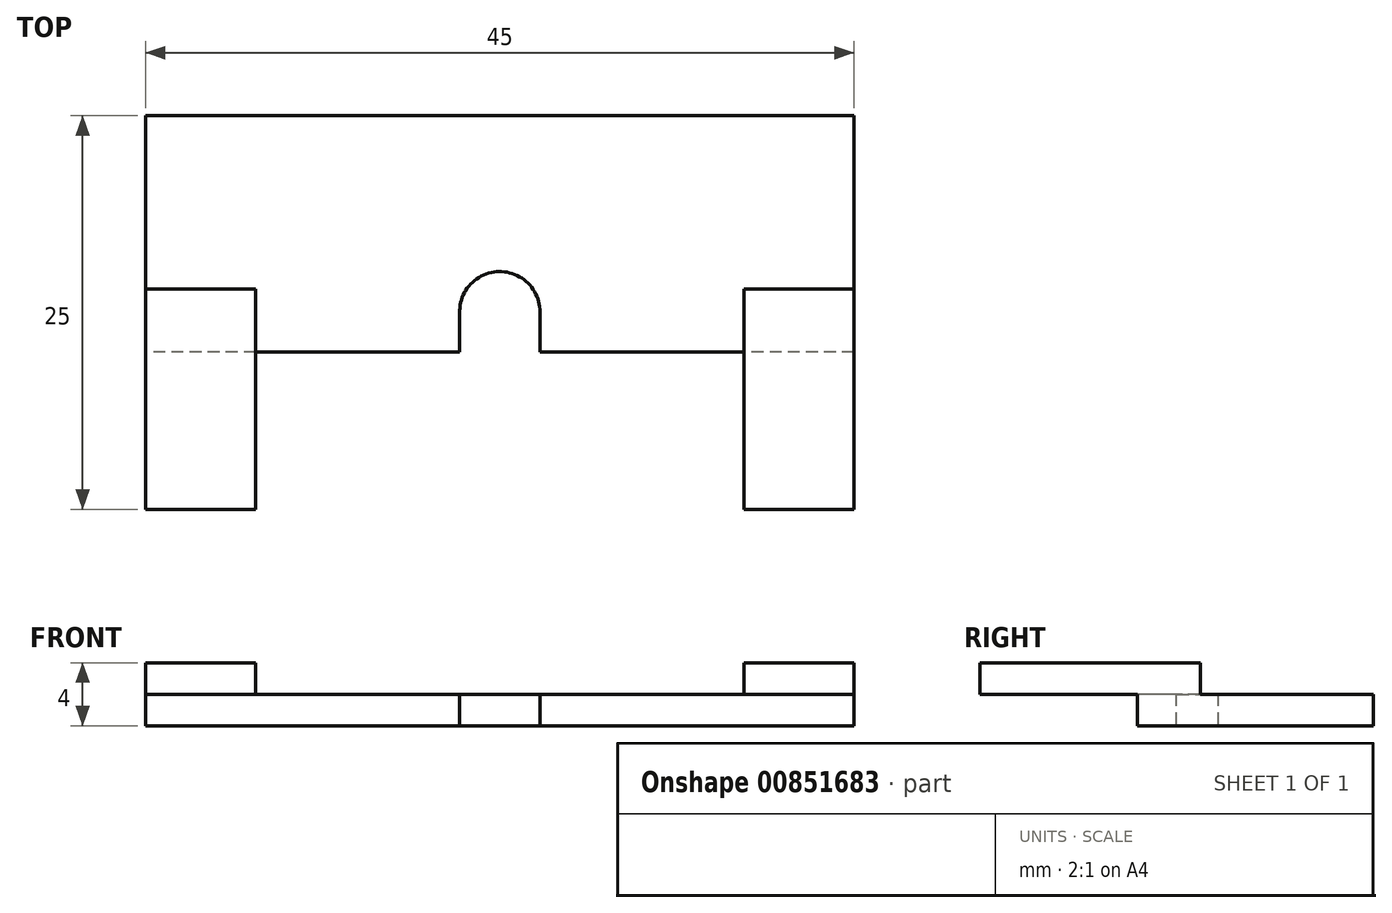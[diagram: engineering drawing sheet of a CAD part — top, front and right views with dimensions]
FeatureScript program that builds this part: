
annotation { "Feature Type Name" : "Feature", "Feature Type Description" : "" }
export const myFeature = defineFeature(function(context is Context, id is Id, definition is map)
    precondition{}
    {
        {
            var Q0;
            Q0=qCreatedBy(makeId("Top.planeOp"),FACE);
            var sketch = newSketch(context, id + "F0", { "sketchPlane" : qUnion([Q0])});
            skLineSegment(sketch, "E0.bottom", {"start": v(22.5, -7.5) * mm, "end": v(-22.5, -7.5) * mm});
            skLineSegment(sketch, "E0.top", {"start": v(22.5, 7.5) * mm, "end": v(-22.5, 7.5) * mm});
            skLineSegment(sketch, "E0.left", {"start": v(22.5, -7.5) * mm, "end": v(22.5, 7.5) * mm});
            skLineSegment(sketch, "E0.right", {"start": v(-22.5, -7.5) * mm, "end": v(-22.5, 7.5) * mm});
            skPoint(sketch, "E0.middle", {"position": v(0, 0) * mm});
            skLineSegment(sketch, "E1", {"start": v(0, -7.5) * mm, "end": v(0, -4.95) * mm, "construction": true});
            skArc(sketch, "E2", {"start": v(2.55, -4.97) * mm, "mid": v(-0.04, -2.4) * mm, "end": v(-2.55, -5.05) * mm});
            skLineSegment(sketch, "E3", {"start": v(-2.55, -5.05) * mm, "end": v(-2.55, -7.5) * mm});
            skLineSegment(sketch, "E4", {"start": v(2.55, -4.97) * mm, "end": v(2.55, -7.5) * mm});
            skSolve(sketch);
        }
        {
            var Q0;
            Q0=makeQuery(id+"F0.imprint","IMPRINT",FACE,{"disambiguationData":[TD([[makeQuery(id+"F0.imprint","IMPRINT",EDGE,{"derivedFrom":sQuery(id+"F0.wireOp",EDGE,"E0.top")}),1.0]])]});
            extrude(context, id + "F1", {"entities" : qUnion([Q0]), "depth" : 2 * mm, "offsetDistance" : 25 * mm});
        }
        {
            var Q0;
            Q0=makeQuery(id+"F1.opExtrude","CAP_FACE",FACE,{"disambiguationData":[OSD([sQuery(id+"F0.wireOp",EDGE,"E0.bottom"),sQuery(id+"F0.wireOp",EDGE,"E0.top"),sQuery(id+"F0.wireOp",EDGE,"E0.left"),sQuery(id+"F0.wireOp",EDGE,"E0.right"),sQuery(id+"F0.wireOp",EDGE,"E2"),sQuery(id+"F0.wireOp",EDGE,"E3"),sQuery(id+"F0.wireOp",EDGE,"E4")])],"isStart":false});
            var sketch = newSketch(context, id + "F2", { "sketchPlane" : qUnion([Q0])});
            skLineSegment(sketch, "E5.bottom", {"start": v(-22.5, -3.5) * mm, "end": v(-15.5, -3.5) * mm});
            skLineSegment(sketch, "E5.top", {"start": v(-22.5, -17.5) * mm, "end": v(-15.5, -17.5) * mm});
            skLineSegment(sketch, "E5.left", {"start": v(-22.5, -3.5) * mm, "end": v(-22.5, -17.5) * mm});
            skLineSegment(sketch, "E5.right", {"start": v(-15.5, -3.5) * mm, "end": v(-15.5, -17.5) * mm});
            skLineSegment(sketch, "E6", {"start": v(-22.5, -7.5) * mm, "end": v(-15.5, -7.5) * mm});
            skLineSegment(sketch, "E7.MirrorCS", {"start": v(22.5, -3.5) * mm, "end": v(22.5, -17.5) * mm});
            skLineSegment(sketch, "E8.MirrorCS", {"start": v(22.5, -3.5) * mm, "end": v(15.5, -3.5) * mm});
            skLineSegment(sketch, "E9.MirrorCS", {"start": v(15.5, -3.5) * mm, "end": v(15.5, -17.5) * mm});
            skLineSegment(sketch, "E10.MirrorCS", {"start": v(22.5, -17.5) * mm, "end": v(15.5, -17.5) * mm});
            skSolve(sketch);
        }
        {
            var Q0;
            {var subQ0=sQuery(id+"F2.wireOp",EDGE,"E5.top");Q0=makeQuery(id+"F2.imprint","IMPRINT",FACE,{"disambiguationData":[TD([[makeQuery(id+"F2.imprint","IMPRINT",EDGE,{"derivedFrom":subQ0}),1.0]])]});}
            var Q1;
            {var subQ0=sQuery(id+"F2.wireOp",EDGE,"E5.bottom");Q1=makeQuery(id+"F2.imprint","IMPRINT",FACE,{"disambiguationData":[TD([[makeQuery(id+"F2.imprint","IMPRINT",EDGE,{"derivedFrom":subQ0}),-1.0]])]});}
            var Q2;
            {var subQ4=sQuery(id+"F2.wireOp",EDGE,"E10.MirrorCS");Q2=makeQuery(id+"F2.imprint","IMPRINT",FACE,{"disambiguationData":[TD([[makeQuery(id+"F2.imprint","IMPRINT",EDGE,{"derivedFrom":subQ4}),-1.0]])]});}
            var Q3;
            {var subQ5=sQuery(id+"F2.wireOp",EDGE,"E8.MirrorCS");Q3=makeQuery(id+"F2.imprint","IMPRINT",FACE,{"disambiguationData":[TD([[makeQuery(id+"F2.imprint","IMPRINT",EDGE,{"derivedFrom":subQ5}),1.0]])]});}
            extrude(context, id + "F3", {"entities" : qUnion([Q0, Q1, Q2, Q3]), "operationType" : NewBodyOperationType.ADD, "depth" : 2 * mm, "offsetDistance" : 25 * mm});
        }
    });
